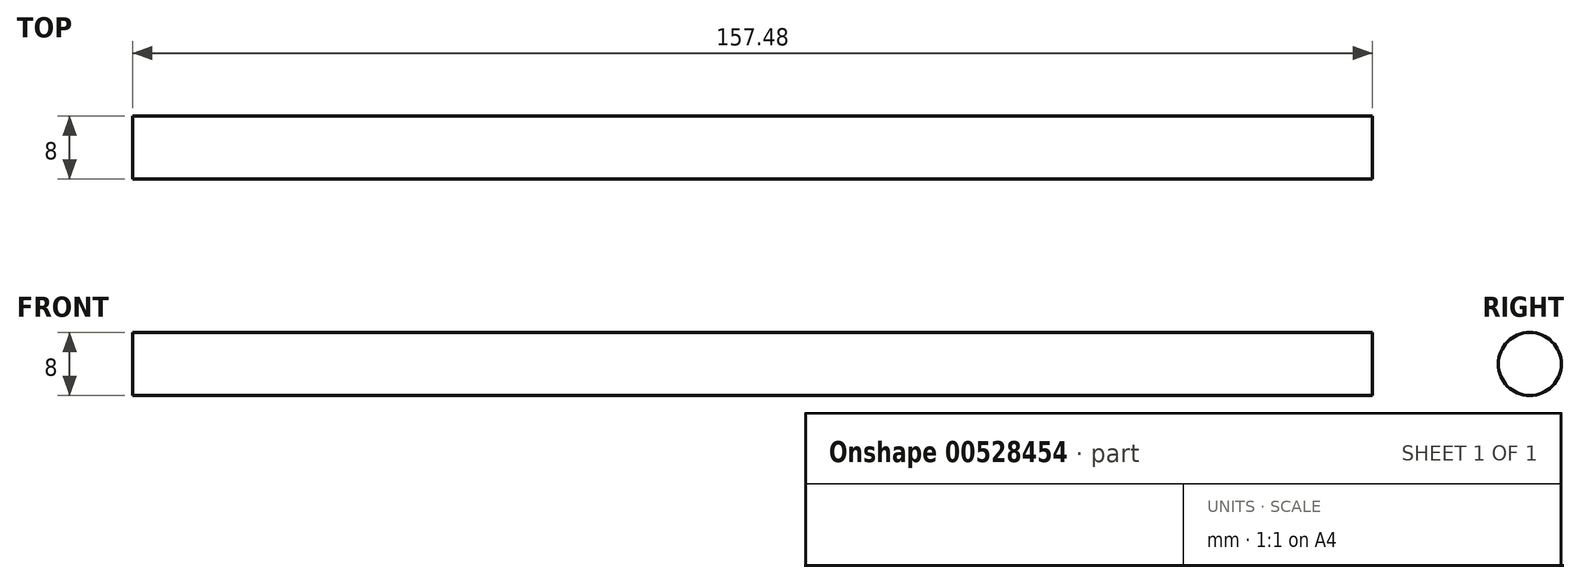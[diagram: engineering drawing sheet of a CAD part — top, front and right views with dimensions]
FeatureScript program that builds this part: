
annotation { "Feature Type Name" : "Feature", "Feature Type Description" : "" }
export const myFeature = defineFeature(function(context is Context, id is Id, definition is map)
    precondition{}
    {
        {
            var Q0;
            Q0=qCreatedBy(makeId("Right.planeOp"),FACE);
            var sketch = newSketch(context, id + "F0", { "sketchPlane" : qUnion([Q0])});
            skCircle(sketch, "E0", {"center": v(0, 0) * mm, "radius": 4 * mm});
            skSolve(sketch);
        }
        {
            var Q0;
            Q0 = qSketchRegion(id + "F0", true);
            extrude(context, id + "F1", {"entities" : qUnion([Q0]), "endBound" : BoundingType.SYMMETRIC, "depth" : 157.48 * mm, "offsetDistance" : 25.4 * mm});
        }
    });
